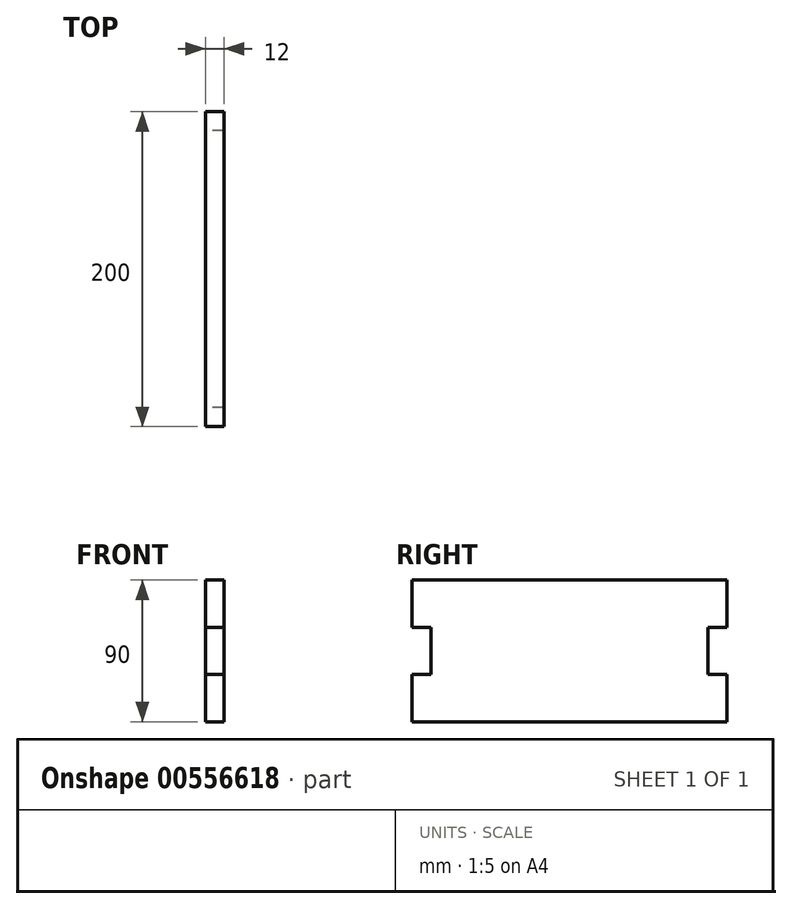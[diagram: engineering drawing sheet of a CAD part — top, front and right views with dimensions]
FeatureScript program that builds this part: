
annotation { "Feature Type Name" : "Feature", "Feature Type Description" : "" }
export const myFeature = defineFeature(function(context is Context, id is Id, definition is map)
    precondition{}
    {
        {
            var Q0;
            Q0=qCreatedBy(makeId("Right.planeOp"),FACE);
            var sketch = newSketch(context, id + "F0", { "sketchPlane" : qUnion([Q0])});
            skLineSegment(sketch, "E0", {"start": v(0, 0) * mm, "end": v(0, 30) * mm});
            skLineSegment(sketch, "E1", {"start": v(0, 30) * mm, "end": v(12, 30) * mm});
            skLineSegment(sketch, "E2", {"start": v(12, 30) * mm, "end": v(12, 60) * mm});
            skLineSegment(sketch, "E3", {"start": v(12, 60) * mm, "end": v(0, 60) * mm});
            skLineSegment(sketch, "E4", {"start": v(0, 60) * mm, "end": v(0, 90) * mm});
            skLineSegment(sketch, "E5", {"start": v(0, 90) * mm, "end": v(100, 90) * mm});
            skLineSegment(sketch, "E6", {"start": v(100, 90) * mm, "end": v(100, 0) * mm});
            skLineSegment(sketch, "E7", {"start": v(100, 0) * mm, "end": v(0, 0) * mm});
            skLineSegment(sketch, "E8.MirrorCS", {"start": v(100, 0) * mm, "end": v(200, 0) * mm});
            skLineSegment(sketch, "E9.MirrorCS", {"start": v(200, 60) * mm, "end": v(200, 90) * mm});
            skLineSegment(sketch, "E10.MirrorCS", {"start": v(200, 30) * mm, "end": v(188, 30) * mm});
            skLineSegment(sketch, "E11.MirrorCS", {"start": v(200, 0) * mm, "end": v(200, 30) * mm});
            skLineSegment(sketch, "E12.MirrorCS", {"start": v(188, 60) * mm, "end": v(200, 60) * mm});
            skLineSegment(sketch, "E13.MirrorCS", {"start": v(200, 90) * mm, "end": v(100, 90) * mm});
            skLineSegment(sketch, "E14.MirrorCS", {"start": v(188, 30) * mm, "end": v(188, 60) * mm});
            skSolve(sketch);
        }
        {
            var Q0;
            Q0=makeQuery(id+"F0.imprint","IMPRINT",FACE,{"disambiguationData":[TD([[makeQuery(id+"F0.imprint","IMPRINT",EDGE,{"derivedFrom":sQuery(id+"F0.wireOp",EDGE,"E6")}),1.0]])]});
            var Q1;
            Q1=makeQuery(id+"F0.imprint","IMPRINT",FACE,{"disambiguationData":[TD([[makeQuery(id+"F0.imprint","IMPRINT",EDGE,{"derivedFrom":sQuery(id+"F0.wireOp",EDGE,"E0")}),-1.0]])]});
            extrude(context, id + "F1", {"entities" : qUnion([Q0, Q1]), "endBound" : BoundingType.SYMMETRIC, "depth" : 12 * mm, "offsetDistance" : 25 * mm});
        }
    });
